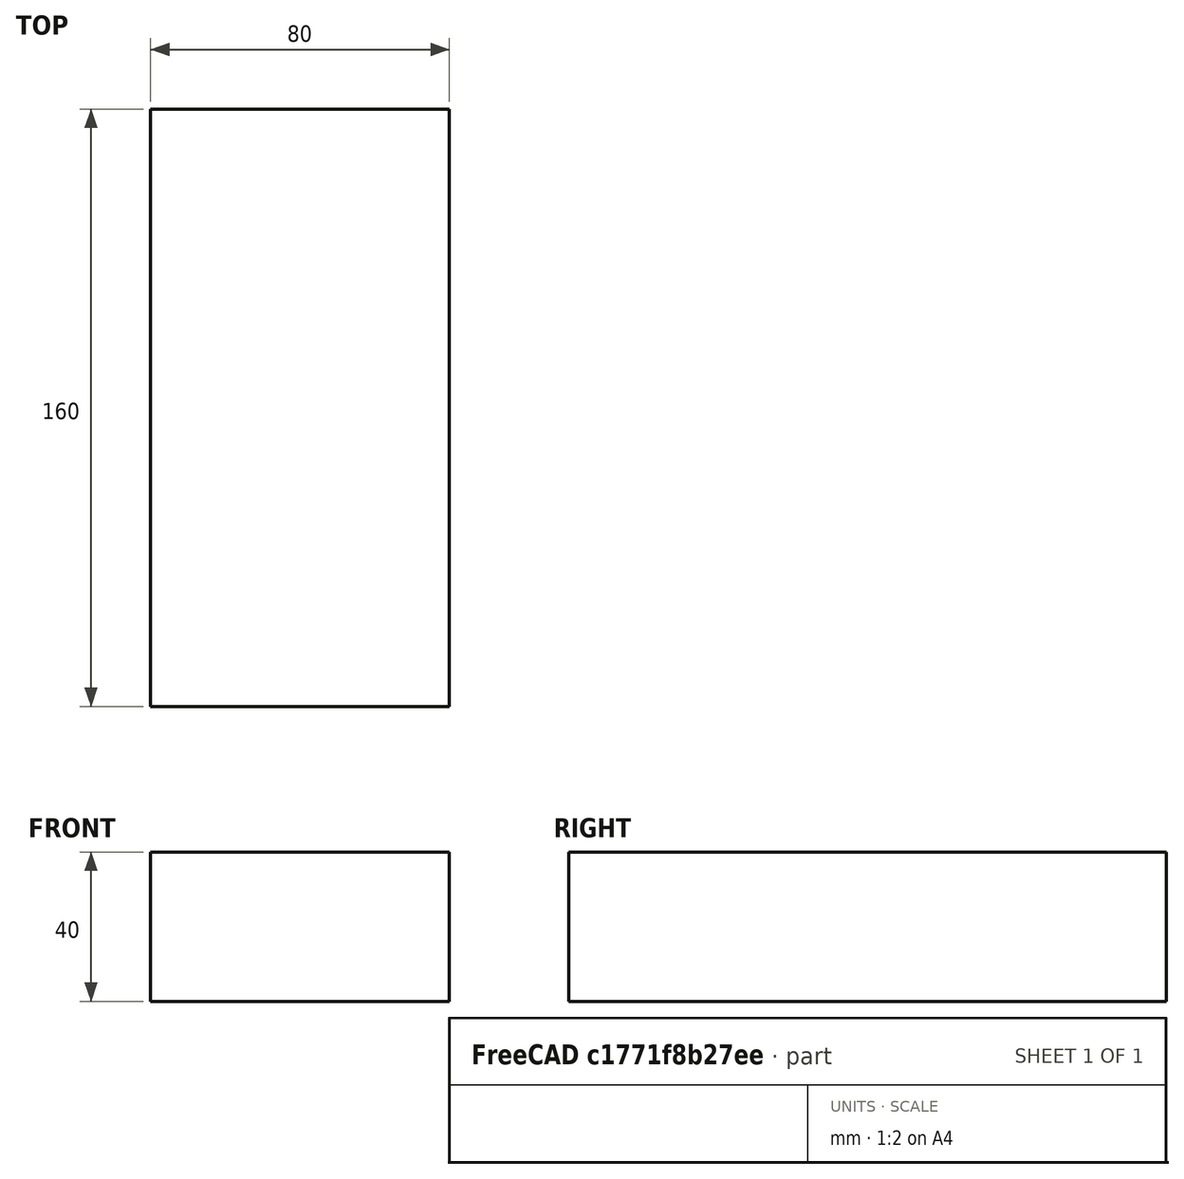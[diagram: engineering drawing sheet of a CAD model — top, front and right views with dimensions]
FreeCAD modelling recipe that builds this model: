
FCSTD DOCUMENT  (FreeCAD 0.18R4 (GitTag))
Label: Box-B
License: All rights reserved
LicenseURL: http://en.wikipedia.org/wiki/All_rights_reserved
objects: Sketcher::SketchObject×1, PartDesign::Pad×1, PartDesign::Body×1
note: 4 computed .brp shape members not serialized (recipe doc carries the construction recipe); baked Part::Feature solids carry a one-line shape summary decoded from their .brp

FEATURE [Sketcher::SketchObject] Sketch
  MapMode = 5
  Support = -> [XY_Plane]
  sketch-geometry (4):
    g0: LineSegment StartX=0 StartY=0 StartZ=0 EndX=-80 EndY=0 EndZ=0
    g1: LineSegment StartX=-80 StartY=0 StartZ=0 EndX=-80 EndY=160 EndZ=0
    g2: LineSegment StartX=-80 StartY=160 StartZ=0 EndX=0 EndY=160 EndZ=0
    g3: LineSegment StartX=0 StartY=160 StartZ=0 EndX=0 EndY=0 EndZ=0
  constraints (10):
    c: Coincident(g0,g1)
    c: Coincident(g1,g2)
    c: Coincident(g2,g3)
    c: Coincident(g3,g0)
    c: Horizontal(g2)
    c: Vertical(g1)
    c: Distance(g0) = 80
    c: Distance(g1) = 160
    c: Tangent(g3,g-2)
    c: Tangent(g0,g-1)
FEATURE [PartDesign::Pad] Pad
  Length = 40
  Length2 = 100
  Profile = -> Sketch
  Type = 0
FEATURE [PartDesign::Body] Body
  Group = -> [Sketch,Pad]
  Origin = -> Origin
  Tip = -> Pad
